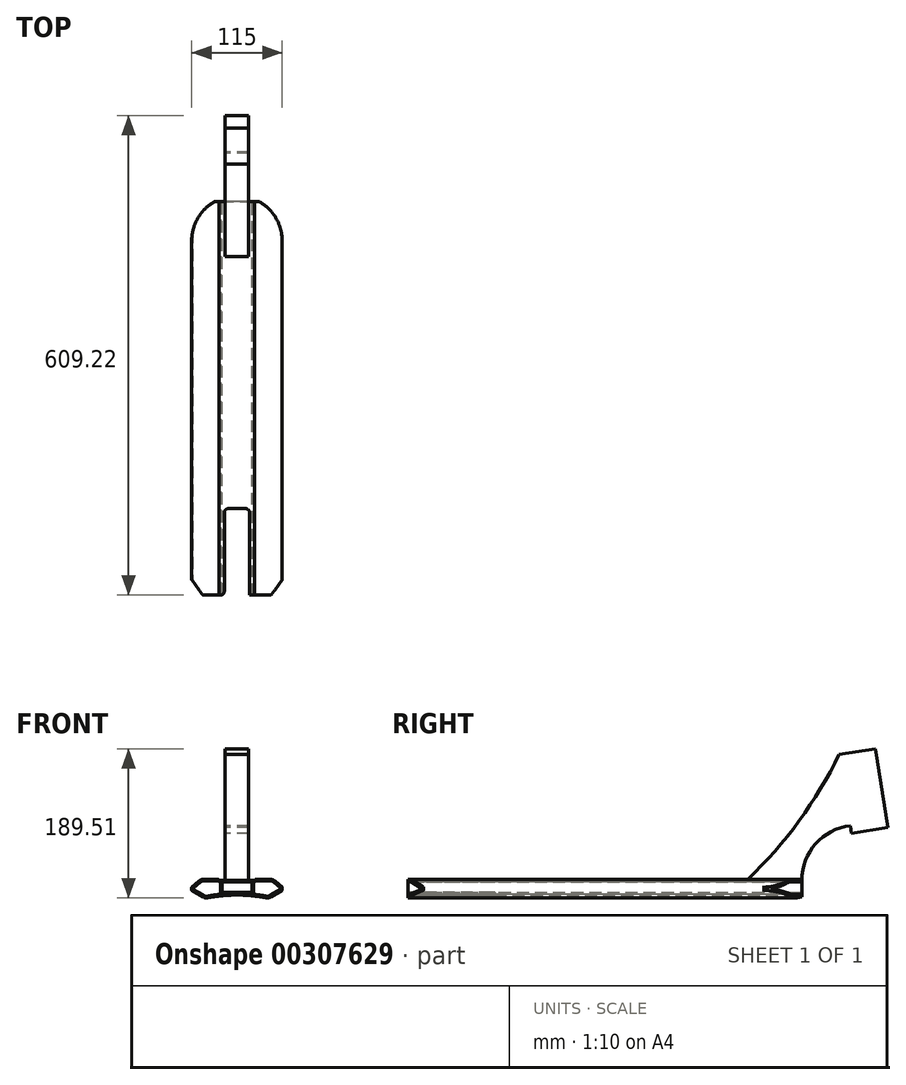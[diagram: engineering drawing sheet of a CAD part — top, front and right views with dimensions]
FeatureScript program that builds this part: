
annotation { "Feature Type Name" : "Feature", "Feature Type Description" : "" }
export const myFeature = defineFeature(function(context is Context, id is Id, definition is map)
    precondition{}
    {
        {
            var Q0;
            Q0=qCreatedBy(makeId("Front.planeOp"),FACE);
            var sketch = newSketch(context, id + "F0", { "sketchPlane" : qUnion([Q0])});
            skLineSegment(sketch, "E0", {"start": v(0, 0) * mm, "end": v(0, 41.19) * mm, "construction": true});
            skLineSegment(sketch, "E1", {"start": v(0, 21.3) * mm, "end": v(22.5, 21.3) * mm});
            skLineSegment(sketch, "E2", {"start": v(22.5, 21.3) * mm, "end": v(22.5, 22.6) * mm});
            skLineSegment(sketch, "E3", {"start": v(22.5, 22.6) * mm, "end": v(45.58, 22.6) * mm});
            skLineSegment(sketch, "E4", {"start": v(45.58, 22.6) * mm, "end": v(57.5, 12.6) * mm});
            skLineSegment(sketch, "E5", {"start": v(57.5, 12.6) * mm, "end": v(57.5, 8.6) * mm});
            skLineSegment(sketch, "E6", {"start": v(57.5, 8.6) * mm, "end": v(40.18, -1.4) * mm});
            skLineSegment(sketch, "E7.MirrorCS", {"start": v(0, 21.3) * mm, "end": v(-22.5, 21.3) * mm});
            skLineSegment(sketch, "E8.MirrorCS", {"start": v(-22.5, 21.3) * mm, "end": v(-22.5, 22.6) * mm});
            skLineSegment(sketch, "E9.MirrorCS", {"start": v(-22.5, 22.6) * mm, "end": v(-45.58, 22.6) * mm});
            skLineSegment(sketch, "E10.MirrorCS", {"start": v(-45.58, 22.6) * mm, "end": v(-57.5, 12.6) * mm});
            skLineSegment(sketch, "E11.MirrorCS", {"start": v(-57.5, 12.6) * mm, "end": v(-57.5, 8.6) * mm});
            skLineSegment(sketch, "E12.MirrorCS", {"start": v(-57.5, 8.6) * mm, "end": v(-40.18, -1.4) * mm});
            skArc(sketch, "E13", {"start": v(40.18, -1.4) * mm, "mid": v(0, 2.67) * mm, "end": v(-40.18, -1.4) * mm});
            skSolve(sketch);
        }
        {
            var Q0;
            Q0 = qSketchRegion(id + "F0", true);
            extrude(context, id + "F1", {"entities" : qUnion([Q0]), "endBound" : BoundingType.SYMMETRIC, "depth" : 500 * mm});
        }
        {
            var Q0;
            Q0=qCreatedBy(makeId("Front.planeOp"),FACE);
            var sketch = newSketch(context, id + "F2", { "sketchPlane" : qUnion([Q0])});
            skLineSegment(sketch, "E14.bottom", {"start": v(-19, 19.3) * mm, "end": v(19, 19.3) * mm});
            skLineSegment(sketch, "E14.top", {"start": v(-19, 6.3) * mm, "end": v(19, 6.3) * mm});
            skLineSegment(sketch, "E14.left", {"start": v(-19, 19.3) * mm, "end": v(-19, 6.3) * mm});
            skLineSegment(sketch, "E14.right", {"start": v(19, 19.3) * mm, "end": v(19, 6.3) * mm});
            skSolve(sketch);
        }
        {
            var Q0;
            Q0 = qSketchRegion(id + "F2", true);
            extrude(context, id + "F3", {"entities" : qUnion([Q0]), "operationType" : NewBodyOperationType.REMOVE, "endBound" : BoundingType.SYMMETRIC, "depth" : 500 * mm});
        }
        {
            var Q0;
            Q0=makeQuery(id+"F1.opExtrude","SWEPT_EDGE",EDGE,{"disambiguationData":[OSD([sQuery(id+"F0.wireOp",EDGE,"E8.MirrorCS"),sQuery(id+"F0.wireOp",EDGE,"E9.MirrorCS")])]});
            var Q1;
            Q1=makeQuery(id+"F1.opExtrude","SWEPT_EDGE",EDGE,{"disambiguationData":[OSD([sQuery(id+"F0.wireOp",EDGE,"E2"),sQuery(id+"F0.wireOp",EDGE,"E3")])]});
            fillet(context, id + "F4", {"entities" : qUnion([Q0, Q1]), "radius" : 2 * mm, "tangentPropagation" : true, "allowEdgeOverflow" : false});
        }
        {
            var Q0;
            Q0=makeQuery(id+"F1.opExtrude","SWEPT_EDGE",EDGE,{"disambiguationData":[OSD([sQuery(id+"F0.wireOp",EDGE,"E9.MirrorCS"),sQuery(id+"F0.wireOp",EDGE,"E10.MirrorCS")])]});
            var Q1;
            Q1=makeQuery(id+"F1.opExtrude","SWEPT_EDGE",EDGE,{"disambiguationData":[OSD([sQuery(id+"F0.wireOp",EDGE,"E3"),sQuery(id+"F0.wireOp",EDGE,"E4")])]});
            var Q2;
            Q2=makeQuery(id+"F1.opExtrude","SWEPT_EDGE",EDGE,{"disambiguationData":[OSD([sQuery(id+"F0.wireOp",EDGE,"E12.MirrorCS"),sQuery(id+"F0.wireOp",EDGE,"E13")])]});
            var Q3;
            Q3=makeQuery(id+"F1.opExtrude","SWEPT_EDGE",EDGE,{"disambiguationData":[OSD([sQuery(id+"F0.wireOp",EDGE,"E6"),sQuery(id+"F0.wireOp",EDGE,"E13")])]});
            fillet(context, id + "F5", {"entities" : qUnion([Q0, Q1, Q2, Q3]), "radius" : 9 * mm, "tangentPropagation" : true, "allowEdgeOverflow" : false});
        }
        {
            var Q0;
            Q0=makeQuery(id+"F1.opExtrude","SWEPT_EDGE",EDGE,{"disambiguationData":[OSD([sQuery(id+"F0.wireOp",EDGE,"E4"),sQuery(id+"F0.wireOp",EDGE,"E5")])]});
            var Q1;
            Q1=makeQuery(id+"F1.opExtrude","SWEPT_EDGE",EDGE,{"disambiguationData":[OSD([sQuery(id+"F0.wireOp",EDGE,"E5"),sQuery(id+"F0.wireOp",EDGE,"E6")])]});
            var Q2;
            Q2=makeQuery(id+"F1.opExtrude","SWEPT_EDGE",EDGE,{"disambiguationData":[OSD([sQuery(id+"F0.wireOp",EDGE,"E10.MirrorCS"),sQuery(id+"F0.wireOp",EDGE,"E11.MirrorCS")])]});
            var Q3;
            Q3=makeQuery(id+"F1.opExtrude","SWEPT_EDGE",EDGE,{"disambiguationData":[OSD([sQuery(id+"F0.wireOp",EDGE,"E11.MirrorCS"),sQuery(id+"F0.wireOp",EDGE,"E12.MirrorCS")])]});
            fillet(context, id + "F6", {"entities" : qUnion([Q0, Q1, Q2, Q3]), "radius" : 1 * mm, "tangentPropagation" : true, "allowEdgeOverflow" : false});
        }
        {
            var Q0;
            Q0=makeQuery(id+"F1.opExtrude","CAP_FACE",FACE,{"disambiguationData":[OSD([sQuery(id+"F0.wireOp",EDGE,"E1"),sQuery(id+"F0.wireOp",EDGE,"E2"),sQuery(id+"F0.wireOp",EDGE,"E3"),sQuery(id+"F0.wireOp",EDGE,"E4"),sQuery(id+"F0.wireOp",EDGE,"E5"),sQuery(id+"F0.wireOp",EDGE,"E6"),sQuery(id+"F0.wireOp",EDGE,"E7.MirrorCS"),sQuery(id+"F0.wireOp",EDGE,"E8.MirrorCS"),sQuery(id+"F0.wireOp",EDGE,"E9.MirrorCS"),sQuery(id+"F0.wireOp",EDGE,"E10.MirrorCS"),sQuery(id+"F0.wireOp",EDGE,"E11.MirrorCS"),sQuery(id+"F0.wireOp",EDGE,"E12.MirrorCS"),sQuery(id+"F0.wireOp",EDGE,"E13")])],"isStart":false});
            var sketch = newSketch(context, id + "F7", { "sketchPlane" : qUnion([Q0])});
            skLineSegment(sketch, "E15.0.0", {"start": v(43.1, 0.28) * mm, "end": v(57, 8.3) * mm});
            skArc(sketch, "E15.0.1", {"start": v(57, 8.3) * mm, "mid": v(57.37, 8.67) * mm, "end": v(57.5, 9.17) * mm});
            skLineSegment(sketch, "E15.0.2", {"start": v(57.5, 9.17) * mm, "end": v(57.5, 12.13) * mm});
            skArc(sketch, "E15.0.3", {"start": v(57.5, 12.13) * mm, "mid": v(57.4, 12.55) * mm, "end": v(57.14, 12.9) * mm});
            skLineSegment(sketch, "E15.0.4", {"start": v(57.14, 12.9) * mm, "end": v(48.1, 20.49) * mm});
            skArc(sketch, "E15.0.5", {"start": v(48.1, 20.49) * mm, "mid": v(45.38, 22.05) * mm, "end": v(42.3, 22.6) * mm});
            skLineSegment(sketch, "E15.0.6", {"start": v(42.3, 22.6) * mm, "end": v(24.37, 22.6) * mm});
            skArc(sketch, "E15.0.7", {"start": v(24.37, 22.6) * mm, "mid": v(23.23, 22.24) * mm, "end": v(22.5, 21.3) * mm});
            skLineSegment(sketch, "E15.0.8", {"start": v(22.5, 21.3) * mm, "end": v(-22.5, 21.3) * mm});
            skArc(sketch, "E15.0.9", {"start": v(-22.5, 21.3) * mm, "mid": v(-23.23, 22.24) * mm, "end": v(-24.37, 22.6) * mm});
            skLineSegment(sketch, "E15.0.10", {"start": v(-24.37, 22.6) * mm, "end": v(-42.3, 22.6) * mm});
            skArc(sketch, "E15.0.11", {"start": v(-42.3, 22.6) * mm, "mid": v(-45.38, 22.05) * mm, "end": v(-48.1, 20.49) * mm});
            skLineSegment(sketch, "E15.0.12", {"start": v(-48.1, 20.49) * mm, "end": v(-57.14, 12.9) * mm});
            skArc(sketch, "E15.0.13", {"start": v(-57.14, 12.9) * mm, "mid": v(-57.4, 12.55) * mm, "end": v(-57.5, 12.13) * mm});
            skLineSegment(sketch, "E15.0.14", {"start": v(-57.5, 12.13) * mm, "end": v(-57.5, 9.17) * mm});
            skArc(sketch, "E15.0.15", {"start": v(-57.5, 9.17) * mm, "mid": v(-57.37, 8.67) * mm, "end": v(-57, 8.3) * mm});
            skLineSegment(sketch, "E15.0.16", {"start": v(-57, 8.3) * mm, "end": v(-43.1, 0.28) * mm});
            skArc(sketch, "E15.0.17", {"start": v(-43.1, 0.28) * mm, "mid": v(-40.12, -0.8) * mm, "end": v(-36.94, -0.77) * mm});
            skArc(sketch, "E15.0.18", {"start": v(-36.94, -0.77) * mm, "mid": v(0, 2.67) * mm, "end": v(36.94, -0.77) * mm});
            skArc(sketch, "E15.0.19", {"start": v(36.94, -0.77) * mm, "mid": v(40.12, -0.8) * mm, "end": v(43.1, 0.28) * mm});
            skArc(sketch, "E16.0", {"start": v(-37.3, 1.2) * mm, "mid": v(0, 4.67) * mm, "end": v(37.3, 1.2) * mm});
            skArc(sketch, "E16.1", {"start": v(-42.1, 2.01) * mm, "mid": v(-39.78, 1.17) * mm, "end": v(-37.3, 1.2) * mm});
            skLineSegment(sketch, "E16.2", {"start": v(-24.37, 20.6) * mm, "end": v(-42.3, 20.6) * mm});
            skArc(sketch, "E16.3", {"start": v(-42.3, 20.6) * mm, "mid": v(-44.7, 20.17) * mm, "end": v(-46.8, 18.95) * mm});
            skLineSegment(sketch, "E16.4", {"start": v(-46.8, 18.95) * mm, "end": v(-55.76, 11.44) * mm});
            skLineSegment(sketch, "E16.5", {"start": v(-55.61, 9.81) * mm, "end": v(-42.1, 2.01) * mm});
            skPoint(sketch, "E17.visualSharp", {"position": v(-56.85, 10.53) * mm});
            skArc(sketch, "E17.filletArc", {"start": v(-55.76, 11.44) * mm, "mid": v(-56.1, 10.6) * mm, "end": v(-55.61, 9.81) * mm});
            skLineSegment(sketch, "E18", {"start": v(-21, 3.58) * mm, "end": v(-21, 19.3) * mm});
            skLineSegment(sketch, "E19", {"start": v(-21, 19.3) * mm, "end": v(-22.5, 19.3) * mm});
            skArc(sketch, "E20", {"start": v(-22.5, 19.3) * mm, "mid": v(-23.23, 20.24) * mm, "end": v(-24.37, 20.6) * mm});
            skLineSegment(sketch, "E21.MirrorCS", {"start": v(21, 3.58) * mm, "end": v(21, 19.3) * mm});
            skLineSegment(sketch, "E22.MirrorCS", {"start": v(21, 19.3) * mm, "end": v(22.5, 19.3) * mm});
            skArc(sketch, "E23.MirrorCS", {"start": v(22.5, 19.3) * mm, "mid": v(23.23, 20.24) * mm, "end": v(24.37, 20.6) * mm});
            skLineSegment(sketch, "E24.MirrorCS", {"start": v(24.37, 20.6) * mm, "end": v(42.3, 20.6) * mm});
            skArc(sketch, "E25.MirrorCS", {"start": v(42.3, 20.6) * mm, "mid": v(44.7, 20.17) * mm, "end": v(46.8, 18.95) * mm});
            skLineSegment(sketch, "E26.MirrorCS", {"start": v(46.8, 18.95) * mm, "end": v(55.76, 11.44) * mm});
            skArc(sketch, "E27.MirrorCS", {"start": v(55.76, 11.44) * mm, "mid": v(56.1, 10.6) * mm, "end": v(55.61, 9.81) * mm});
            skLineSegment(sketch, "E28.MirrorCS", {"start": v(55.61, 9.81) * mm, "end": v(42.1, 2.01) * mm});
            skArc(sketch, "E29.MirrorCS", {"start": v(42.1, 2.01) * mm, "mid": v(39.78, 1.17) * mm, "end": v(37.3, 1.2) * mm});
            skArc(sketch, "E30.MirrorCS", {"start": v(37.3, 1.2) * mm, "mid": v(29.18, 2.55) * mm, "end": v(21, 3.58) * mm});
            skArc(sketch, "E31.trimOffspring", {"start": v(-21, 3.58) * mm, "mid": v(-29.18, 2.55) * mm, "end": v(-37.3, 1.2) * mm});
            skSolve(sketch);
        }
        {
            var Q0;
            Q0=makeQuery(id+"F7.imprint","IMPRINT",FACE,{"disambiguationData":[TD([[makeQuery(id+"F7.imprint","IMPRINT",EDGE,{"derivedFrom":sQuery(id+"F7.wireOp",EDGE,"E16.1")}),1.0]])]});
            var Q1;
            Q1=makeQuery(id+"F7.imprint","IMPRINT",FACE,{"disambiguationData":[TD([[makeQuery(id+"F7.imprint","IMPRINT",EDGE,{"derivedFrom":sQuery(id+"F7.wireOp",EDGE,"E21.MirrorCS")}),-1.0]])]});
            extrude(context, id + "F8", {"entities" : qUnion([Q0, Q1]), "operationType" : NewBodyOperationType.REMOVE, "endBound" : BoundingType.THROUGH_ALL, "oppositeDirection" : true, "depth" : 25 * mm});
        }
        {
            var Q0;
            Q0=qCreatedBy(makeId("Top.planeOp"),FACE);
            var sketch = newSketch(context, id + "F9", { "sketchPlane" : qUnion([Q0])});
            skArc(sketch, "E32", {"start": v(57.5, 200.06) * mm, "mid": v(-0.02, 257.5) * mm, "end": v(-57.5, 200.03) * mm});
            skLineSegment(sketch, "E33", {"start": v(57.5, 280.06) * mm, "end": v(-57.5, 280.06) * mm});
            skLineSegment(sketch, "E34", {"start": v(57.5, 200.06) * mm, "end": v(57.5, 280.06) * mm});
            skLineSegment(sketch, "E35", {"start": v(-57.5, 280.06) * mm, "end": v(-57.5, 200.03) * mm});
            skSolve(sketch);
        }
        {
            var Q0;
            Q0 = qSketchRegion(id + "F9", true);
            extrude(context, id + "F10", {"entities" : qUnion([Q0]), "operationType" : NewBodyOperationType.REMOVE, "depth" : 25 * mm, "hasSecondDirection" : true, "secondDirectionOppositeDirection" : true, "secondDirectionDepth" : 25 * mm});
        }
        {
            var Q0;
            Q0=qCreatedBy(makeId("Top.planeOp"),FACE);
            var sketch = newSketch(context, id + "F11", { "sketchPlane" : qUnion([Q0])});
            skLineSegment(sketch, "E36", {"start": v(-43.3, -250) * mm, "end": v(-68, -216) * mm});
            skLineSegment(sketch, "E37", {"start": v(-68, -216) * mm, "end": v(-68, -380) * mm});
            skLineSegment(sketch, "E38", {"start": v(-68, -380) * mm, "end": v(68, -380) * mm});
            skLineSegment(sketch, "E39", {"start": v(68, -380) * mm, "end": v(68, -216) * mm});
            skLineSegment(sketch, "E40", {"start": v(68, -216) * mm, "end": v(43.3, -250) * mm});
            skLineSegment(sketch, "E41", {"start": v(43.3, -250) * mm, "end": v(16, -250) * mm});
            skLineSegment(sketch, "E42", {"start": v(16, -250) * mm, "end": v(16, -140) * mm});
            skLineSegment(sketch, "E43", {"start": v(16, -140) * mm, "end": v(-16, -140) * mm});
            skLineSegment(sketch, "E44", {"start": v(-16, -140) * mm, "end": v(-16, -250) * mm});
            skLineSegment(sketch, "E45", {"start": v(-16, -250) * mm, "end": v(-43.3, -250) * mm});
            skSolve(sketch);
        }
        {
            var Q0;
            Q0 = qSketchRegion(id + "F11", true);
            extrude(context, id + "F12", {"entities" : qUnion([Q0]), "operationType" : NewBodyOperationType.REMOVE, "depth" : 25 * mm});
        }
        {
            var Q0;
            {var subQ2=sQuery(id+"F11.wireOp",EDGE,"E44");Q0=makeQuery(id+"F12.boolean.opBoolean","COPY",EDGE,{"disambiguationData":[TD([makeQuery(id+"F3.boolean.opBoolean","COPY",FACE,{"derivedFrom":makeQuery(id+"F3.opExtrude","SWEPT_FACE",FACE,{"disambiguationData":[OSD([sQuery(id+"F2.wireOp",EDGE,"E14.bottom")])]})})])],"derivedFrom":makeQuery(id+"F12.opExtrude","SWEPT_EDGE",EDGE,{"disambiguationData":[OSD([subQ2,sQuery(id+"F11.wireOp",EDGE,"E45")])]})});}
            var Q1;
            {var subQ2=sQuery(id+"F11.wireOp",EDGE,"E42");Q1=makeQuery(id+"F12.boolean.opBoolean","COPY",EDGE,{"disambiguationData":[TD([makeQuery(id+"F3.boolean.opBoolean","COPY",FACE,{"derivedFrom":makeQuery(id+"F3.opExtrude","SWEPT_FACE",FACE,{"disambiguationData":[OSD([sQuery(id+"F2.wireOp",EDGE,"E14.bottom")])]})})])],"derivedFrom":makeQuery(id+"F12.opExtrude","SWEPT_EDGE",EDGE,{"disambiguationData":[OSD([sQuery(id+"F11.wireOp",EDGE,"E41"),subQ2])]})});}
            var Q2;
            {var subQ0=sQuery(id+"F0.wireOp",EDGE,"E13");var subQ1=sQuery(id+"F11.wireOp",EDGE,"E44");Q2=makeQuery(id+"F12.boolean.opBoolean","COPY",EDGE,{"disambiguationData":[TD([makeQuery(id+"F1.opExtrude","SWEPT_FACE",FACE,{"disambiguationData":[OSD([subQ0])]})])],"derivedFrom":makeQuery(id+"F12.opExtrude","SWEPT_EDGE",EDGE,{"disambiguationData":[OSD([subQ1,sQuery(id+"F11.wireOp",EDGE,"E45")])]})});}
            var Q3;
            {var subQ0=sQuery(id+"F0.wireOp",EDGE,"E13");var subQ1=sQuery(id+"F11.wireOp",EDGE,"E42");Q3=makeQuery(id+"F12.boolean.opBoolean","COPY",EDGE,{"disambiguationData":[TD([makeQuery(id+"F1.opExtrude","SWEPT_FACE",FACE,{"disambiguationData":[OSD([subQ0])]})])],"derivedFrom":makeQuery(id+"F12.opExtrude","SWEPT_EDGE",EDGE,{"disambiguationData":[OSD([sQuery(id+"F11.wireOp",EDGE,"E41"),subQ1])]})});}
            var Q4;
            {var subQ0=sQuery(id+"F11.wireOp",EDGE,"E43");var subQ1=sQuery(id+"F11.wireOp",EDGE,"E44");Q4=makeQuery(id+"F12.boolean.opBoolean","COPY",EDGE,{"disambiguationData":[TD([makeQuery(id+"F3.boolean.opBoolean","COPY",FACE,{"derivedFrom":makeQuery(id+"F3.opExtrude","SWEPT_FACE",FACE,{"disambiguationData":[OSD([sQuery(id+"F2.wireOp",EDGE,"E14.bottom")])]})})])],"derivedFrom":makeQuery(id+"F12.opExtrude","SWEPT_EDGE",EDGE,{"disambiguationData":[OSD([subQ0,subQ1])]})});}
            var Q5;
            {var subQ0=sQuery(id+"F11.wireOp",EDGE,"E43");var subQ1=sQuery(id+"F11.wireOp",EDGE,"E44");Q5=makeQuery(id+"F12.boolean.opBoolean","COPY",EDGE,{"disambiguationData":[TD([makeQuery(id+"F1.opExtrude","SWEPT_FACE",FACE,{"disambiguationData":[OSD([sQuery(id+"F0.wireOp",EDGE,"E13")])]})])],"derivedFrom":makeQuery(id+"F12.opExtrude","SWEPT_EDGE",EDGE,{"disambiguationData":[OSD([subQ0,subQ1])]})});}
            var Q6;
            {var subQ0=sQuery(id+"F11.wireOp",EDGE,"E42");var subQ1=sQuery(id+"F11.wireOp",EDGE,"E43");Q6=makeQuery(id+"F12.boolean.opBoolean","COPY",EDGE,{"disambiguationData":[TD([makeQuery(id+"F3.boolean.opBoolean","COPY",FACE,{"derivedFrom":makeQuery(id+"F3.opExtrude","SWEPT_FACE",FACE,{"disambiguationData":[OSD([sQuery(id+"F2.wireOp",EDGE,"E14.bottom")])]})})])],"derivedFrom":makeQuery(id+"F12.opExtrude","SWEPT_EDGE",EDGE,{"disambiguationData":[OSD([subQ0,subQ1])]})});}
            var Q7;
            {var subQ0=sQuery(id+"F11.wireOp",EDGE,"E43");var subQ1=sQuery(id+"F11.wireOp",EDGE,"E42");Q7=makeQuery(id+"F12.boolean.opBoolean","COPY",EDGE,{"disambiguationData":[TD([makeQuery(id+"F1.opExtrude","SWEPT_FACE",FACE,{"disambiguationData":[OSD([sQuery(id+"F0.wireOp",EDGE,"E13")])]})])],"derivedFrom":makeQuery(id+"F12.opExtrude","SWEPT_EDGE",EDGE,{"disambiguationData":[OSD([subQ1,subQ0])]})});}
            fillet(context, id + "F13", {"entities" : qUnion([Q0, Q1, Q2, Q3, Q4, Q5, Q6, Q7]), "radius" : 5 * mm, "tangentPropagation" : true, "allowEdgeOverflow" : false});
        }
        {
            var Q0;
            Q0=qCreatedBy(makeId("Right.planeOp"),FACE);
            var sketch = newSketch(context, id + "F14", { "sketchPlane" : qUnion([Q0])});
            skLineSegment(sketch, "E46", {"start": v(180, 21.3) * mm, "end": v(250, 21.3) * mm});
            skArc(sketch, "E47", {"start": v(180, 21.3) * mm, "mid": v(245.97, 95.95) * mm, "end": v(297.38, 181.3) * mm});
            skArc(sketch, "E48", {"start": v(311.71, 90.8) * mm, "mid": v(267.66, 67.77) * mm, "end": v(250, 21.3) * mm});
            skLineSegment(sketch, "E49", {"start": v(297.38, 181.3) * mm, "end": v(343.38, 188.58) * mm});
            skLineSegment(sketch, "E50", {"start": v(343.38, 188.58) * mm, "end": v(359.22, 88.58) * mm});
            skLineSegment(sketch, "E51", {"start": v(359.22, 88.58) * mm, "end": v(313.22, 81.3) * mm});
            skLineSegment(sketch, "E52", {"start": v(313.22, 81.3) * mm, "end": v(311.71, 90.8) * mm});
            skSolve(sketch);
        }
        {
            var Q0;
            Q0 = qSketchRegion(id + "F14", true);
            extrude(context, id + "F15", {"entities" : qUnion([Q0]), "operationType" : NewBodyOperationType.ADD, "endBound" : BoundingType.SYMMETRIC, "depth" : 30 * mm});
        }
    });
